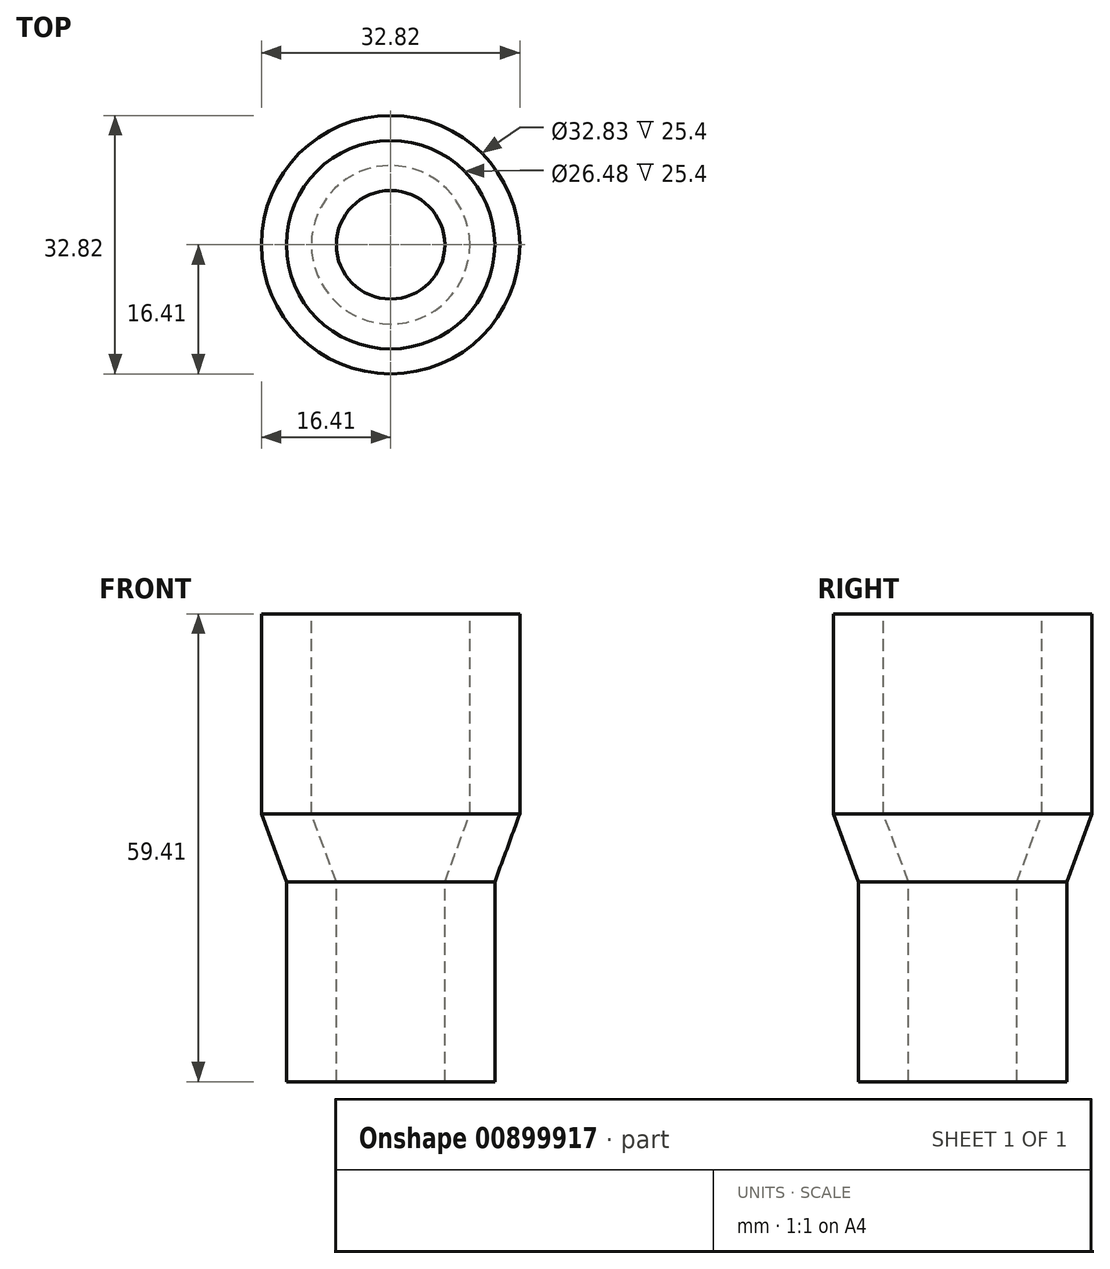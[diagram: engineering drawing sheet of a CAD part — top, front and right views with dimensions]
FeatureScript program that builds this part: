
annotation { "Feature Type Name" : "Feature", "Feature Type Description" : "" }
export const myFeature = defineFeature(function(context is Context, id is Id, definition is map)
    precondition{}
    {
        {
            var Q0;
            Q0=qCreatedBy(makeId("Front.planeOp"),FACE);
            var sketch = newSketch(context, id + "F0", { "sketchPlane" : qUnion([Q0])});
            skLineSegment(sketch, "E0", {"start": v(13.24, 0) * mm, "end": v(13.24, 25.4) * mm});
            skLineSegment(sketch, "E1", {"start": v(13.24, 25.4) * mm, "end": v(16.41, 34.01) * mm});
            skLineSegment(sketch, "E2", {"start": v(16.41, 34.01) * mm, "end": v(16.41, 59.41) * mm});
            skLineSegment(sketch, "E3", {"start": v(16.41, 59.41) * mm, "end": v(10.06, 59.41) * mm});
            skLineSegment(sketch, "E4", {"start": v(10.06, 59.41) * mm, "end": v(10.06, 34.01) * mm});
            skLineSegment(sketch, "E5", {"start": v(10.06, 34.01) * mm, "end": v(6.89, 25.4) * mm});
            skLineSegment(sketch, "E6", {"start": v(6.89, 25.4) * mm, "end": v(6.89, 0) * mm});
            skLineSegment(sketch, "E7", {"start": v(6.89, 0) * mm, "end": v(13.24, 0) * mm});
            skLineSegment(sketch, "E8", {"start": v(0, 0) * mm, "end": v(0, 69.6) * mm, "construction": true});
            skSolve(sketch);
        }
        {
            var Q0;
            Q0 = qConstructionFilter(qBodyType(qCreatedBy(id + "F0" ,EDGE), BodyType.WIRE), ConstructionObject.NO);
            var Q1;
            Q1=sQuery(id+"F0.wireOp",EDGE,"E8");
            revolve(context, id + "F1", {"bodyType" : ToolBodyType.SURFACE, "surfaceOperationType" : NewSurfaceOperationType.NEW, "surfaceEntities" : qUnion([Q0]), "axis" : qUnion([Q1]), "revolveType" : RevolveType.FULL});
        }
    });
